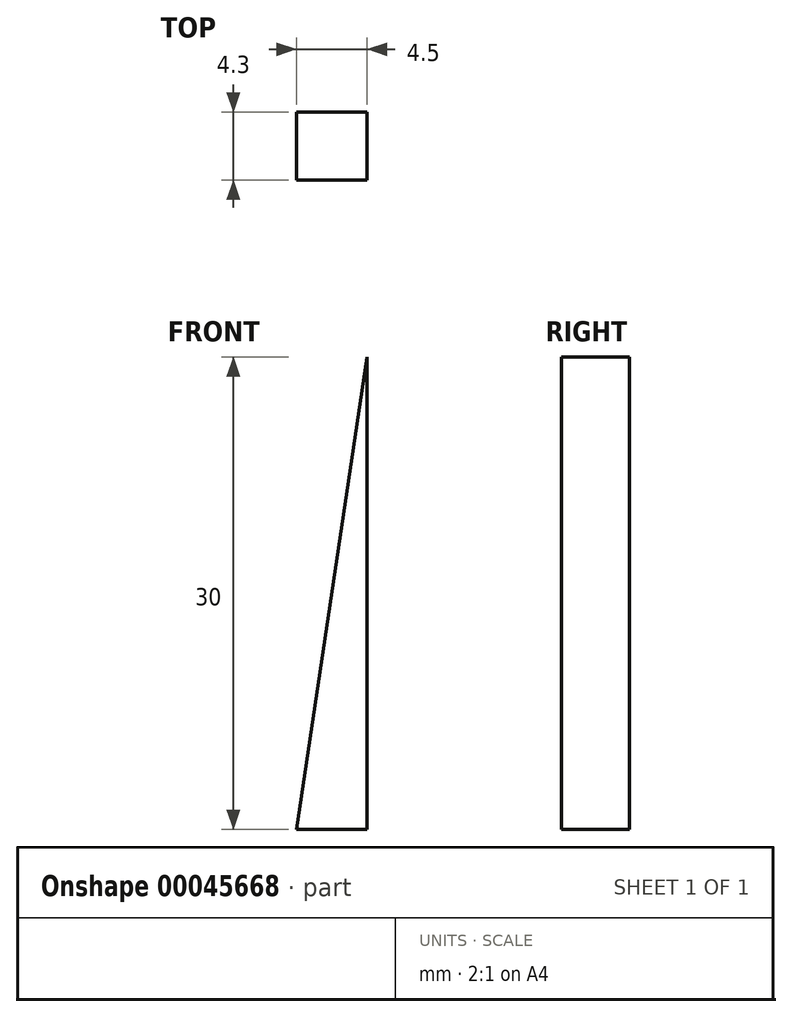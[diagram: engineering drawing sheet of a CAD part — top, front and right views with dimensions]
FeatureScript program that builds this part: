
annotation { "Feature Type Name" : "Feature", "Feature Type Description" : "" }
export const myFeature = defineFeature(function(context is Context, id is Id, definition is map)
    precondition{}
    {
        {
            var Q0;
            Q0=qCreatedBy(makeId("Front.planeOp"),FACE);
            var sketch = newSketch(context, id + "F0", { "sketchPlane" : qUnion([Q0])});
            skLineSegment(sketch, "E0", {"start": v(-40.98, 28.08) * mm, "end": v(-40.98, -1.92) * mm, "construction": true});
            skLineSegment(sketch, "E1", {"start": v(-40.98, -1.92) * mm, "end": v(-45.48, -1.92) * mm, "construction": true});
            skLineSegment(sketch, "E2", {"start": v(-40.98, 28.08) * mm, "end": v(-40.98, -1.92) * mm});
            skLineSegment(sketch, "E3", {"start": v(-45.48, -1.92) * mm, "end": v(-40.98, 28.08) * mm});
            skLineSegment(sketch, "E4", {"start": v(-45.48, -1.92) * mm, "end": v(-40.98, -1.92) * mm});
            skSolve(sketch);
        }
        {
            var Q0;
            Q0=makeQuery(id+"F0.imprint","IMPRINT",FACE,{"disambiguationData":[TD([[makeQuery(id+"F0.imprint","IMPRINT",EDGE,{"derivedFrom":sQuery(id+"F0.wireOp",EDGE,"E2")}),-1.0]])]});
            extrude(context, id + "F1", {"entities" : qUnion([Q0]), "depth" : 4.3 * mm});
        }
    });
